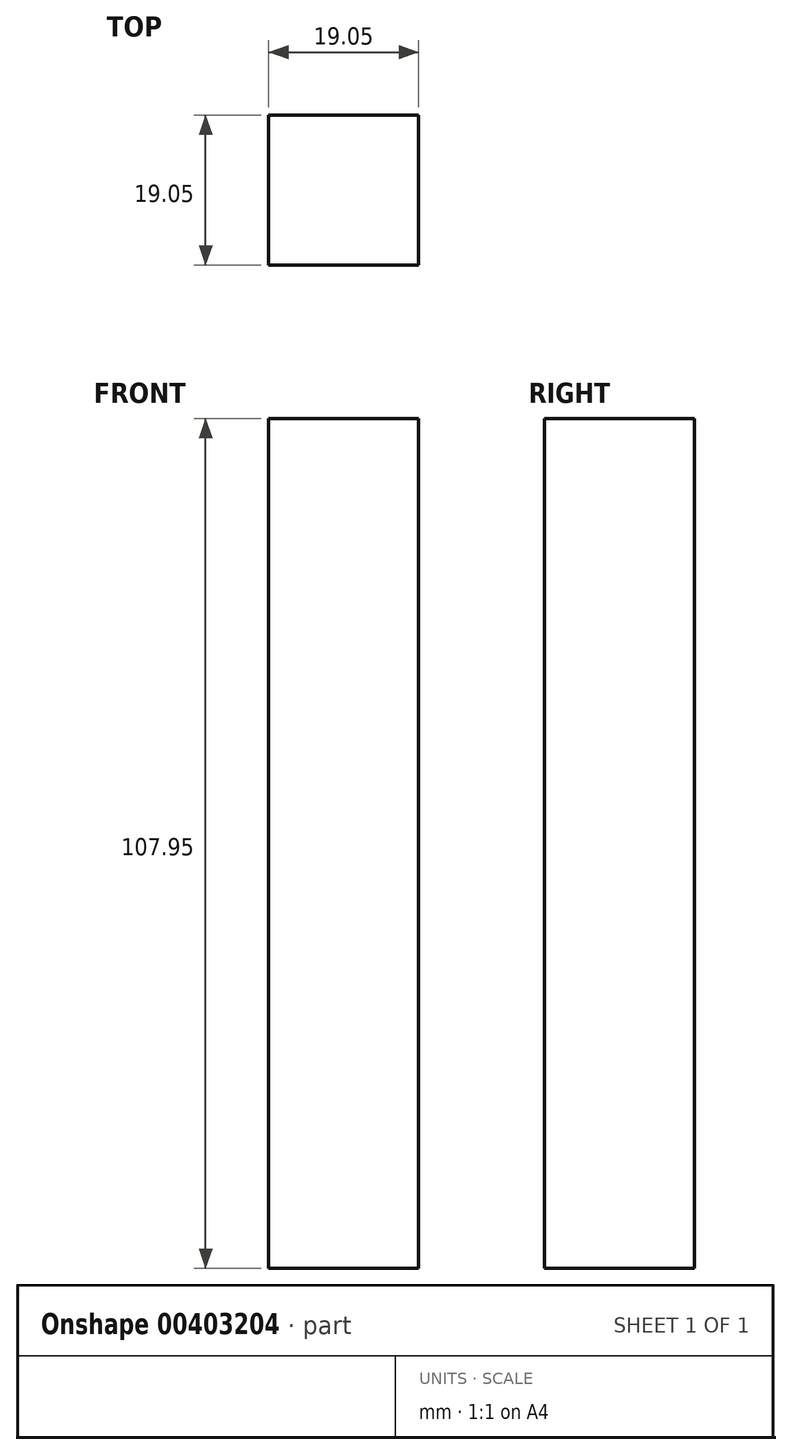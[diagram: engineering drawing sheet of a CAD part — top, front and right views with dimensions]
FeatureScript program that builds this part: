
annotation { "Feature Type Name" : "Feature", "Feature Type Description" : "" }
export const myFeature = defineFeature(function(context is Context, id is Id, definition is map)
    precondition{}
    {
        {
            var Q0;
            Q0=qCreatedBy(makeId("Top.planeOp"),FACE);
            var sketch = newSketch(context, id + "F0", { "sketchPlane" : qUnion([Q0])});
            skLineSegment(sketch, "E0.bottom", {"start": v(0, 0) * mm, "end": v(19.05, 0) * mm});
            skLineSegment(sketch, "E0.top", {"start": v(0, 19.05) * mm, "end": v(19.05, 19.05) * mm});
            skLineSegment(sketch, "E0.left", {"start": v(0, 0) * mm, "end": v(0, 19.05) * mm});
            skLineSegment(sketch, "E0.right", {"start": v(19.05, 0) * mm, "end": v(19.05, 19.05) * mm});
            skSolve(sketch);
        }
        {
            var Q0;
            Q0 = qSketchRegion(id + "F0", true);
            extrude(context, id + "F1", {"entities" : qUnion([Q0]), "depth" : 107.95 * mm});
        }
    });
